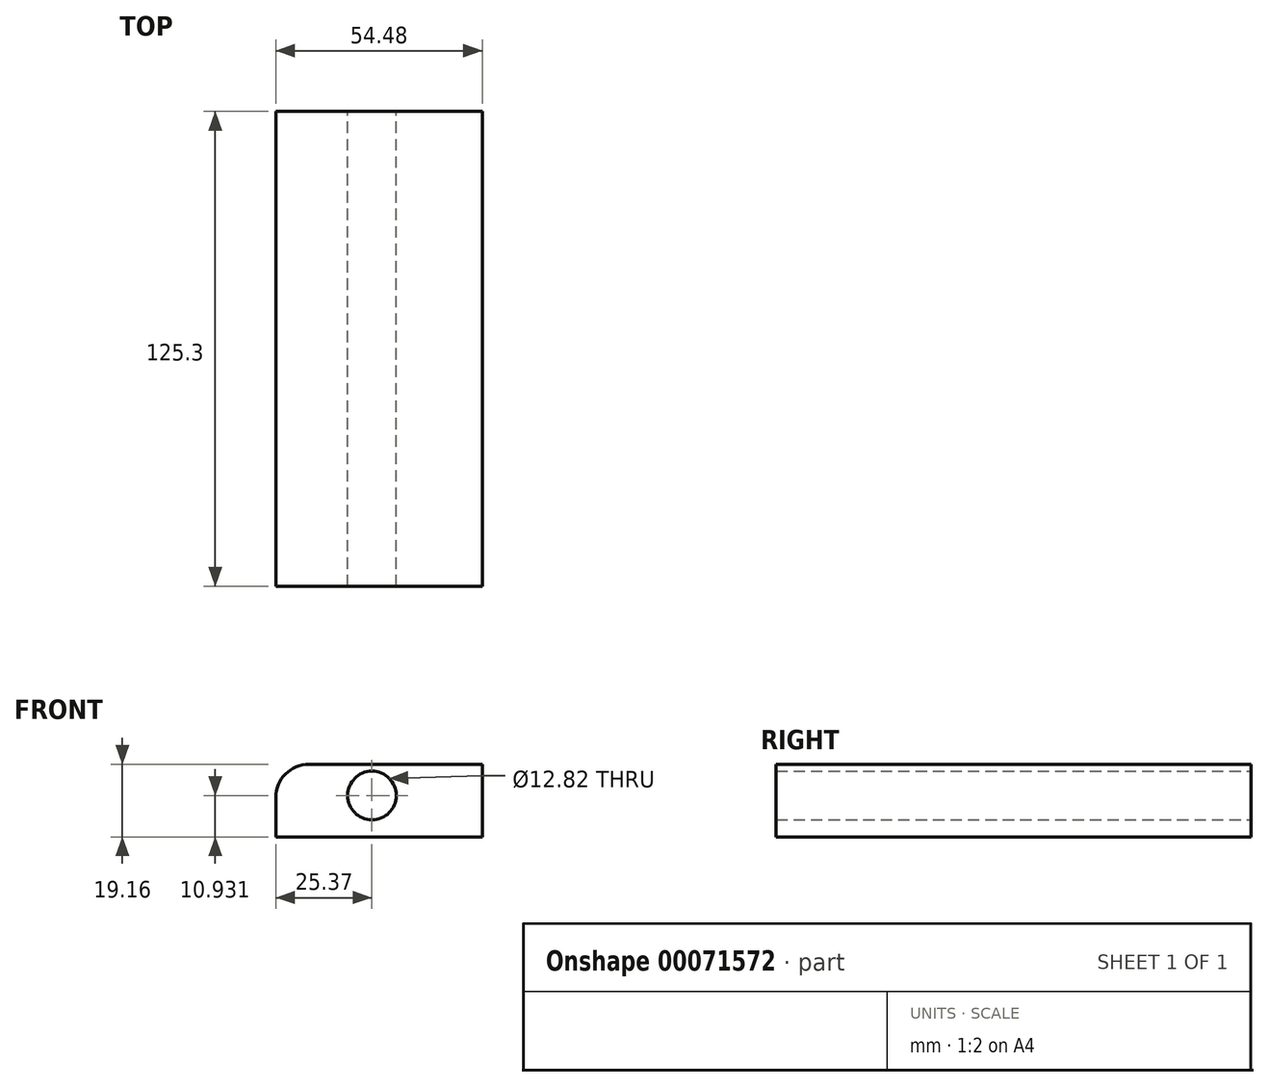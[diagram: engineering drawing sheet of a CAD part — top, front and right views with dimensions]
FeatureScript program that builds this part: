
annotation { "Feature Type Name" : "Feature", "Feature Type Description" : "" }
export const myFeature = defineFeature(function(context is Context, id is Id, definition is map)
    precondition{}
    {
        {
            var Q0;
            Q0=qCreatedBy(makeId("Front.planeOp"),FACE);
            var sketch = newSketch(context, id + "F0", { "sketchPlane" : qUnion([Q0])});
            skLineSegment(sketch, "E0.bottom", {"start": v(-25.37, -54) * mm, "end": v(29.11, -54) * mm});
            skLineSegment(sketch, "E0.top", {"start": v(-25.37, -34.84) * mm, "end": v(29.11, -34.84) * mm});
            skLineSegment(sketch, "E0.left", {"start": v(-25.37, -54) * mm, "end": v(-25.37, -34.84) * mm});
            skLineSegment(sketch, "E0.right", {"start": v(29.11, -54) * mm, "end": v(29.11, -34.84) * mm});
            skCircle(sketch, "E1", {"center": v(0, -43.07) * mm, "radius": 6.4 * mm});
            skSolve(sketch);
        }
        {
            var Q0;
            Q0=makeQuery(id+"F0.imprint","IMPRINT",FACE,{"disambiguationData":[TD([[makeQuery(id+"F0.imprint","IMPRINT",EDGE,{"derivedFrom":sQuery(id+"F0.wireOp",EDGE,"E0.bottom")}),1.0]])]});
            extrude(context, id + "F1", {"entities" : qUnion([Q0]), "depth" : 125.3 * mm});
        }
        {
            var Q0;
            Q0=makeQuery(id+"F1.opExtrude","SWEPT_EDGE",EDGE,{"disambiguationData":[OSD([sQuery(id+"F0.wireOp",EDGE,"E0.top"),sQuery(id+"F0.wireOp",EDGE,"E0.left")])]});
            fillet(context, id + "F2", {"entities" : qUnion([Q0]), "radius" : 8.79 * mm, "tangentPropagation" : true, "allowEdgeOverflow" : false});
        }
    });
